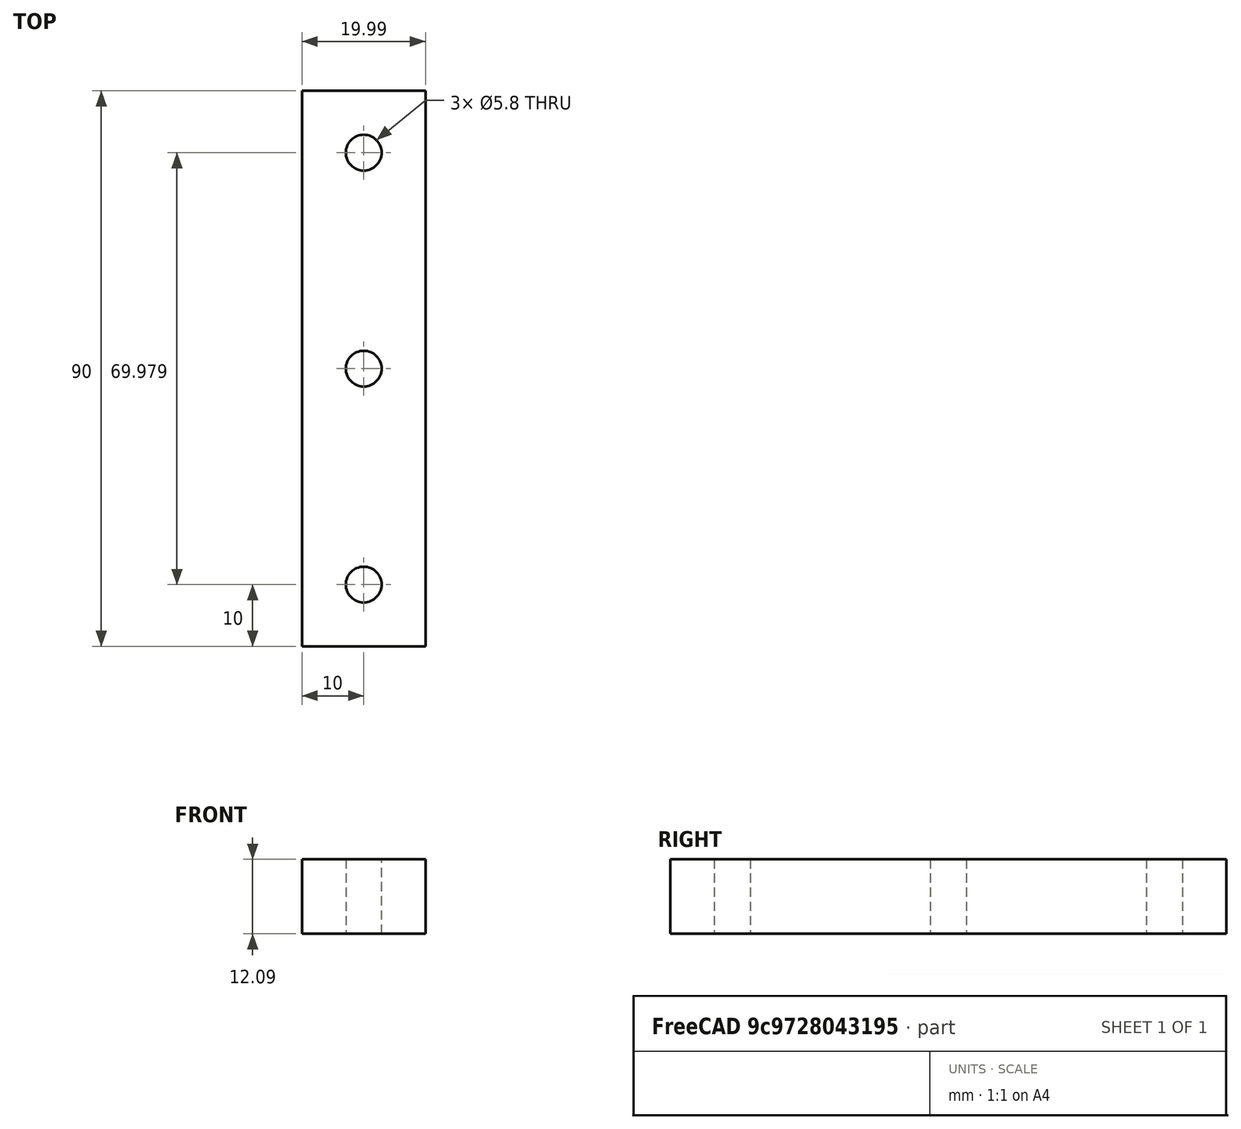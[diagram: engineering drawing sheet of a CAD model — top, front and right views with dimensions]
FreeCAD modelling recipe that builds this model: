
FCSTD DOCUMENT  (FreeCAD 0.20R29410 (Git))
Label: Soporte
License: Creative Commons Attribution-ShareAlike
LicenseURL: http://creativecommons.org/licenses/by-sa/4.0/
objects: Sketcher::SketchObject×2, Part::Extrusion×2, Part::Cut×1
note: 5 computed .brp shape members not serialized (recipe doc carries the construction recipe); baked Part::Feature solids carry a one-line shape summary decoded from their .brp

FEATURE [Sketcher::SketchObject] Sketch009
  FullyConstrained = false
  Placement = pos=(0,0,0) rot=(1,0,0;1.5708rad)
  sketch-geometry (4):
    g0: LineSegment StartX=0 StartY=20.8718 StartZ=0 EndX=0 EndY=8.77665 EndZ=0
    g1: LineSegment StartX=0 StartY=8.77665 StartZ=0 EndX=19.9931 EndY=8.77665 EndZ=0
    g2: LineSegment StartX=19.9931 StartY=20.8718 StartZ=0 EndX=19.9931 EndY=8.77665 EndZ=0
    g3: LineSegment StartX=0 StartY=20.8718 StartZ=0 EndX=19.9931 EndY=20.8718 EndZ=0
  constraints (8):
    c: Vertical(g0)
    c: Coincident(g1,g0)
    c: Horizontal(g1)
    c: Coincident(g2,g1)
    c: Vertical(g2)
    c: Coincident(g3,g0)
    c: Coincident(g3,g2)
    c: Horizontal(g3)
FEATURE [Part::Extrusion] Extrude009  label="Unidor"
  Base = -> Sketch009
  Dir = (0,-1,2e-16)
  DirMode = 2
  FaceMakerClass = Part::FaceMakerBullseye
  LengthFwd = 90
  LengthRev = 0
  Solid = true
  Symmetric = false
FEATURE [Sketcher::SketchObject] Sketch010
  FullyConstrained = false
  MapMode = 5
  Placement = pos=(0,4.6e-15,20.8718) rot=(0,0,1;0rad)
  Support = -> [Extrude009]
  sketch-geometry (4):
    g0: Circle CenterX=10 CenterY=-80 CenterZ=0 NormalX=0 NormalY=0 NormalZ=1 AngleXU=0 Radius=2.9
    g1: Circle CenterX=10 CenterY=-45.0107 CenterZ=0 NormalX=0 NormalY=0 NormalZ=1 AngleXU=0 Radius=2.9
    g2: Circle CenterX=10 CenterY=-10.0214 CenterZ=0 NormalX=0 NormalY=0 NormalZ=1 AngleXU=0 Radius=2.9
    g3: LineSegment StartX=10 StartY=-10.0214 StartZ=0 EndX=10 EndY=-80 EndZ=0
  constraints (7):
    c: Coincident(g3,g2)
    c: Coincident(g3,g0)
    c: Vertical(g3)
    c: Symmetric(g3,g3,g1)
    c: Diameter(g2) = 5.8
    c: Equal(g2,g1)
    c: Equal(g1,g0)
FEATURE [Part::Extrusion] Extrude010  label="Tornillos003"
  Base = -> Sketch010
  Dir = (0,2e-16,1)
  DirMode = 2
  FaceMakerClass = Part::FaceMakerBullseye
  LengthFwd = 20
  LengthRev = 0
  Placement = pos=(0,0,-15) rot=(0,0,1;0rad)
  Solid = true
  Symmetric = false
FEATURE [Part::Cut] Cut003  label="Soporte, Imprimir"
  Base = -> Extrude009
  Placement = pos=(0,90,0) rot=(0,0,1;0rad)
  Refine = true
  Tool = -> Extrude010
